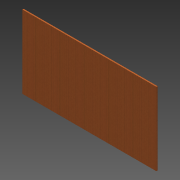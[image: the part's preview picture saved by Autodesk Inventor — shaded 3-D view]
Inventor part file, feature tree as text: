
AUTODESK INVENTOR PART (.ipt)
format: ipt  version: 2013 (Build 170138000, 138)  size: 79,872 bytes
history: native  units: in
note: dims shown in document units (in); Inventor stores cm internally (conversion verified against a paired STEP export)
features: extrude x1, sketch x1
ambient origin geometry x8: Origin, YZ Plane, XZ Plane, XY Plane, X Axis, Y Axis, Z Axis, Center Point
bodies: Solid1 (feature_tree)
feature tree (2):
  extrude  "Extrusion1"  Depth=30.0in
  sketch  "Sketch1"  dims[d0=55.0in d1=30.0in d2=0.5in d3=0.0in]
